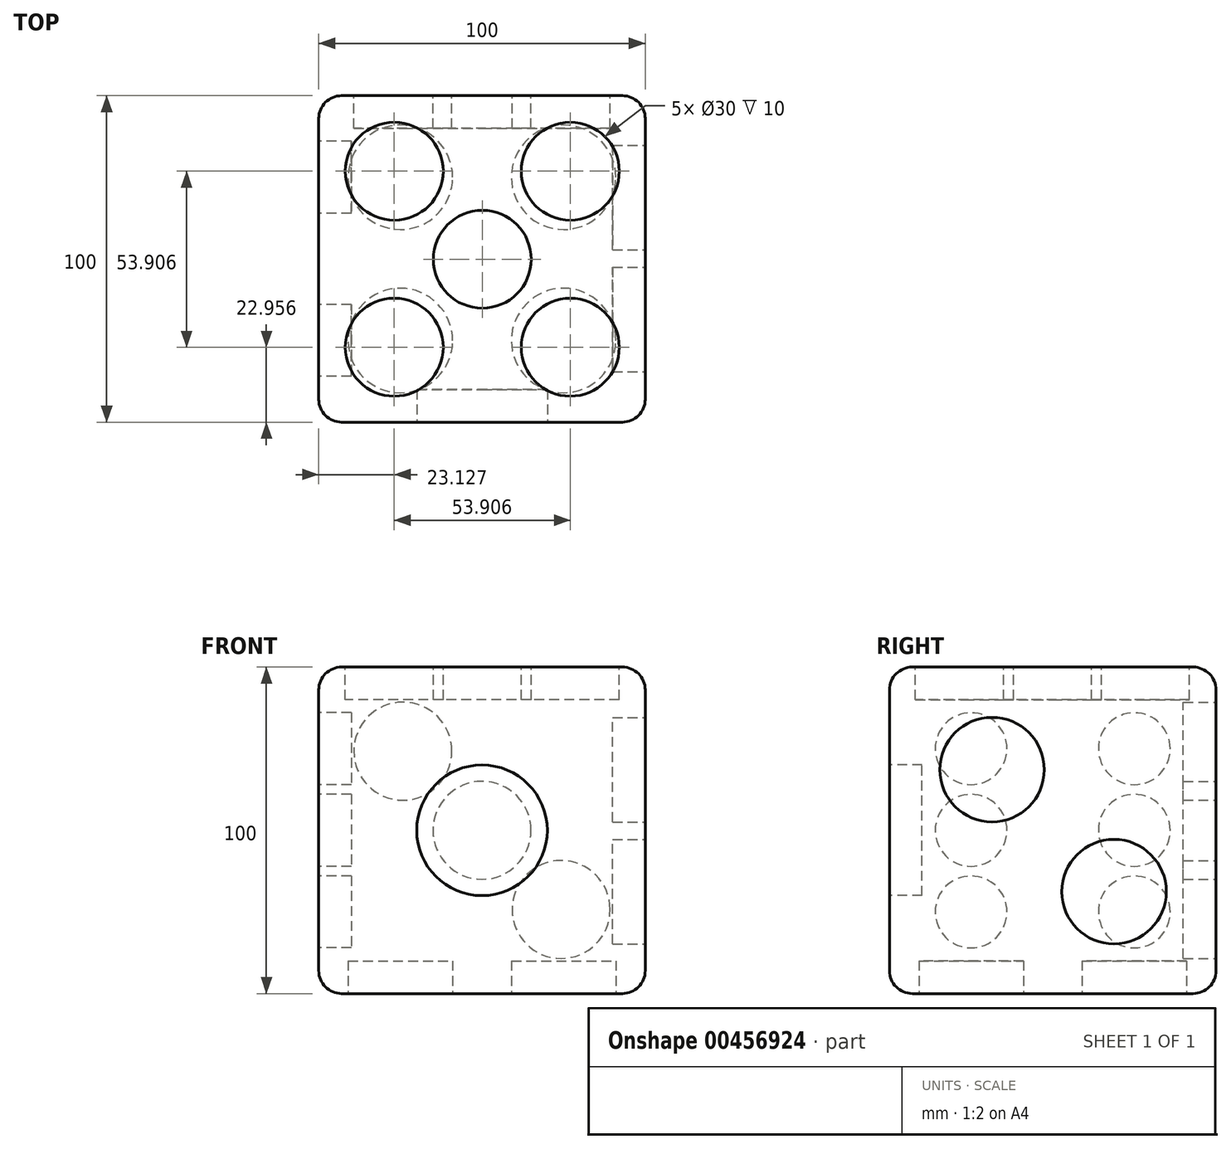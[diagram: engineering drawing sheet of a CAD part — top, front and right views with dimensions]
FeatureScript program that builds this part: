
annotation { "Feature Type Name" : "Feature", "Feature Type Description" : "" }
export const myFeature = defineFeature(function(context is Context, id is Id, definition is map)
    precondition{}
    {
        {
            var Q0;
            Q0=qCreatedBy(makeId("Front.planeOp"),FACE);
            var sketch = newSketch(context, id + "F0", { "sketchPlane" : qUnion([Q0])});
            skLineSegment(sketch, "E0.bottom", {"start": v(-50, 50) * mm, "end": v(50, 50) * mm});
            skLineSegment(sketch, "E0.top", {"start": v(-50, -50) * mm, "end": v(50, -50) * mm});
            skLineSegment(sketch, "E0.left", {"start": v(-50, 50) * mm, "end": v(-50, -50) * mm});
            skLineSegment(sketch, "E0.right", {"start": v(50, 50) * mm, "end": v(50, -50) * mm});
            skPoint(sketch, "E0.middle", {"position": v(0, 0) * mm});
            skSolve(sketch);
        }
        {
            var Q0;
            Q0 = qSketchRegion(id + "F0", true);
            extrude(context, id + "F1", {"entities" : qUnion([Q0]), "depth" : 100 * mm});
        }
        {
            var Q0;
            Q0=makeQuery(id+"F1.opExtrude","SWEPT_FACE",FACE,{"disambiguationData":[OSD([sQuery(id+"F0.wireOp",EDGE,"E0.right")])]});
            var sketch = newSketch(context, id + "F2", { "sketchPlane" : qUnion([Q0])});
            skPoint(sketch, "E1", {"position": v(-68.58, 18.58) * mm});
            skPoint(sketch, "E2", {"position": v(-31.22, -18.78) * mm});
            skCircle(sketch, "E3", {"center": v(-68.58, 18.58) * mm, "radius": 16 * mm});
            skCircle(sketch, "E4", {"center": v(-31.22, -18.78) * mm, "radius": 16 * mm});
            skSolve(sketch);
        }
        {
            var Q0;
            Q0=makeQuery(id+"F1.opExtrude","CAP_FACE",FACE,{"disambiguationData":[OSD([sQuery(id+"F0.wireOp",EDGE,"E0.bottom"),sQuery(id+"F0.wireOp",EDGE,"E0.top"),sQuery(id+"F0.wireOp",EDGE,"E0.left"),sQuery(id+"F0.wireOp",EDGE,"E0.right")])],"isStart":false});
            var sketch = newSketch(context, id + "F3", { "sketchPlane" : qUnion([Q0])});
            skCircle(sketch, "E5", {"center": v(0, 0) * mm, "radius": 20 * mm});
            skSolve(sketch);
        }
        {
            var Q0;
            Q0=makeQuery(id+"F3.imprint","IMPRINT",FACE,{"disambiguationData":[TD([[makeQuery(id+"F3.imprint","IMPRINT",EDGE,{"derivedFrom":sQuery(id+"F3.wireOp",EDGE,"E5")}),1.0]])]});
            var Q1;
            Q1=sQuery(id+"F3.wireOp",EDGE,"E5");
            extrude(context, id + "F4", {"entities" : qUnion([Q0]), "operationType" : NewBodyOperationType.REMOVE, "surfaceEntities" : qUnion([Q1]), "oppositeDirection" : true, "depth" : 10 * mm});
        }
        {
            var Q0;
            Q0=makeQuery(id+"F1.opExtrude","SWEPT_FACE",FACE,{"disambiguationData":[OSD([sQuery(id+"F0.wireOp",EDGE,"E0.bottom")])]});
            var sketch = newSketch(context, id + "F5", { "sketchPlane" : qUnion([Q0])});
            skCircle(sketch, "E6", {"center": v(-26.87, -77.04) * mm, "radius": 15 * mm});
            skCircle(sketch, "E7", {"center": v(27.03, -77.04) * mm, "radius": 15 * mm});
            skCircle(sketch, "E8", {"center": v(27.03, -23.14) * mm, "radius": 15 * mm});
            skCircle(sketch, "E9", {"center": v(-26.87, -23.14) * mm, "radius": 15 * mm});
            skCircle(sketch, "E10", {"center": v(0.08, -50.1) * mm, "radius": 15 * mm});
            skSolve(sketch);
        }
        {
            var Q0;
            Q0 = qSketchRegion(id + "F5", true);
            extrude(context, id + "F6", {"entities" : qUnion([Q0]), "operationType" : NewBodyOperationType.REMOVE, "oppositeDirection" : true, "depth" : 10 * mm});
        }
        {
            var Q0;
            Q0=makeQuery(id+"F1.opExtrude","SWEPT_FACE",FACE,{"disambiguationData":[OSD([sQuery(id+"F0.wireOp",EDGE,"E0.top")])]});
            var sketch = newSketch(context, id + "F7", { "sketchPlane" : qUnion([Q0])});
            skLineSegment(sketch, "E11", {"start": v(0, 100) * mm, "end": v(0, 0) * mm});
            skLineSegment(sketch, "E12", {"start": v(50, 50) * mm, "end": v(-50, 50) * mm});
            skCircle(sketch, "E13", {"center": v(-25, 75) * mm, "radius": 16 * mm});
            skCircle(sketch, "E14", {"center": v(25, 75) * mm, "radius": 16 * mm});
            skCircle(sketch, "E15", {"center": v(25, 25) * mm, "radius": 16 * mm});
            skCircle(sketch, "E16", {"center": v(-25, 25) * mm, "radius": 16 * mm});
            skSolve(sketch);
        }
        {
            var Q0;
            Q0 = qSketchRegion(id + "F7", true);
            extrude(context, id + "F8", {"entities" : qUnion([Q0]), "operationType" : NewBodyOperationType.REMOVE, "oppositeDirection" : true, "depth" : 10 * mm});
        }
        {
            var Q0;
            Q0 = qSketchRegion(id + "F2", true);
            extrude(context, id + "F9", {"entities" : qUnion([Q0]), "operationType" : NewBodyOperationType.REMOVE, "oppositeDirection" : true, "depth" : 10 * mm});
        }
        {
            var Q0;
            Q0=makeQuery(id+"F1.opExtrude","SWEPT_FACE",FACE,{"disambiguationData":[OSD([sQuery(id+"F0.wireOp",EDGE,"E0.left")])]});
            var sketch = newSketch(context, id + "F10", { "sketchPlane" : qUnion([Q0])});
            skPoint(sketch, "E17.endSnap0", {"position": v(75, -25) * mm});
            skCircle(sketch, "E18", {"center": v(75, 25) * mm, "radius": 11 * mm});
            skCircle(sketch, "E19", {"center": v(75, 0) * mm, "radius": 11 * mm});
            skCircle(sketch, "E20", {"center": v(75, -25) * mm, "radius": 11 * mm});
            skCircle(sketch, "E21", {"center": v(25, 25) * mm, "radius": 11 * mm});
            skCircle(sketch, "E22", {"center": v(25, 0) * mm, "radius": 11 * mm});
            skCircle(sketch, "E23", {"center": v(25, -25) * mm, "radius": 11 * mm});
            skSolve(sketch);
        }
        {
            var Q0;
            Q0=makeQuery(id+"F10.imprint","IMPRINT",FACE,{"disambiguationData":[TD([[makeQuery(id+"F10.imprint","IMPRINT",EDGE,{"derivedFrom":sQuery(id+"F10.wireOp",EDGE,"E21")}),1.0]])]});
            var Q1;
            Q1=makeQuery(id+"F10.imprint","IMPRINT",FACE,{"disambiguationData":[TD([[makeQuery(id+"F10.imprint","IMPRINT",EDGE,{"derivedFrom":sQuery(id+"F10.wireOp",EDGE,"E22")}),1.0]])]});
            var Q2;
            Q2=makeQuery(id+"F10.imprint","IMPRINT",FACE,{"disambiguationData":[TD([[makeQuery(id+"F10.imprint","IMPRINT",EDGE,{"derivedFrom":sQuery(id+"F10.wireOp",EDGE,"E23")}),1.0]])]});
            var Q3;
            Q3=makeQuery(id+"F10.imprint","IMPRINT",FACE,{"disambiguationData":[TD([[makeQuery(id+"F10.imprint","IMPRINT",EDGE,{"derivedFrom":sQuery(id+"F10.wireOp",EDGE,"E20")}),1.0]])]});
            var Q4;
            Q4=makeQuery(id+"F10.imprint","IMPRINT",FACE,{"disambiguationData":[TD([[makeQuery(id+"F10.imprint","IMPRINT",EDGE,{"derivedFrom":sQuery(id+"F10.wireOp",EDGE,"E19")}),1.0]])]});
            var Q5;
            Q5=makeQuery(id+"F10.imprint","IMPRINT",FACE,{"disambiguationData":[TD([[makeQuery(id+"F10.imprint","IMPRINT",EDGE,{"derivedFrom":sQuery(id+"F10.wireOp",EDGE,"E18")}),1.0]])]});
            extrude(context, id + "F11", {"entities" : qUnion([Q0, Q1, Q2, Q3, Q4, Q5]), "operationType" : NewBodyOperationType.REMOVE, "oppositeDirection" : true, "depth" : 10 * mm});
        }
        {
            var Q0;
            Q0=makeQuery(id+"F0.imprint","IMPRINT",FACE,{"disambiguationData":[TD([[makeQuery(id+"F0.imprint","IMPRINT",EDGE,{"derivedFrom":sQuery(id+"F0.wireOp",EDGE,"E0.bottom")}),-1.0]])]});
            var sketch = newSketch(context, id + "F12", { "sketchPlane" : qUnion([Q0])});
            skCircle(sketch, "E24", {"center": v(-24.24, 24.24) * mm, "radius": 15 * mm});
            skCircle(sketch, "E25", {"center": v(0, 0) * mm, "radius": 15 * mm});
            skCircle(sketch, "E26", {"center": v(24.24, -24.24) * mm, "radius": 15 * mm});
            skSolve(sketch);
        }
        {
            var Q0;
            Q0=makeQuery(id+"F12.imprint","IMPRINT",FACE,{"disambiguationData":[TD([[makeQuery(id+"F12.imprint","IMPRINT",EDGE,{"derivedFrom":sQuery(id+"F12.wireOp",EDGE,"E25")}),1.0]])]});
            var Q1;
            Q1=makeQuery(id+"F12.imprint","IMPRINT",FACE,{"disambiguationData":[TD([[makeQuery(id+"F12.imprint","IMPRINT",EDGE,{"derivedFrom":sQuery(id+"F12.wireOp",EDGE,"E24")}),1.0]])]});
            var Q2;
            Q2=makeQuery(id+"F12.imprint","IMPRINT",FACE,{"disambiguationData":[TD([[makeQuery(id+"F12.imprint","IMPRINT",EDGE,{"derivedFrom":sQuery(id+"F12.wireOp",EDGE,"E26")}),1.0]])]});
            var Q3;
            Q3=sQuery(id+"F12.wireOp",EDGE,"E24");
            var Q4;
            Q4=sQuery(id+"F12.wireOp",EDGE,"E25");
            var Q5;
            Q5=sQuery(id+"F12.wireOp",EDGE,"E26");
            extrude(context, id + "F13", {"entities" : qUnion([Q0, Q1, Q2]), "operationType" : NewBodyOperationType.REMOVE, "surfaceEntities" : qUnion([Q3, Q4, Q5]), "depth" : 10 * mm});
        }
        {
            var Q0;
            Q0=makeQuery(id+"F1.opExtrude","SWEPT_EDGE",EDGE,{"disambiguationData":[OSD([sQuery(id+"F0.wireOp",EDGE,"E0.bottom"),sQuery(id+"F0.wireOp",EDGE,"E0.left")])]});
            var Q1;
            Q1=makeQuery(id+"F1.opExtrude","CAP_EDGE",EDGE,{"disambiguationData":[OSD([sQuery(id+"F0.wireOp",EDGE,"E0.top")])],"isStart":false});
            var Q2;
            Q2=makeQuery(id+"F1.opExtrude","CAP_EDGE",EDGE,{"disambiguationData":[OSD([sQuery(id+"F0.wireOp",EDGE,"E0.bottom")])],"isStart":false});
            var Q3;
            Q3=makeQuery(id+"F1.opExtrude","CAP_EDGE",EDGE,{"disambiguationData":[OSD([sQuery(id+"F0.wireOp",EDGE,"E0.left")])],"isStart":false});
            var Q4;
            Q4=makeQuery(id+"F1.opExtrude","CAP_EDGE",EDGE,{"disambiguationData":[OSD([sQuery(id+"F0.wireOp",EDGE,"E0.right")])],"isStart":false});
            var Q5;
            Q5=makeQuery(id+"F1.opExtrude","SWEPT_EDGE",EDGE,{"disambiguationData":[OSD([sQuery(id+"F0.wireOp",EDGE,"E0.top"),sQuery(id+"F0.wireOp",EDGE,"E0.right")])]});
            var Q6;
            Q6=makeQuery(id+"F1.opExtrude","CAP_EDGE",EDGE,{"disambiguationData":[OSD([sQuery(id+"F0.wireOp",EDGE,"E0.right")])],"isStart":true});
            var Q7;
            Q7=makeQuery(id+"F1.opExtrude","SWEPT_EDGE",EDGE,{"disambiguationData":[OSD([sQuery(id+"F0.wireOp",EDGE,"E0.bottom"),sQuery(id+"F0.wireOp",EDGE,"E0.right")])]});
            var Q8;
            Q8=makeQuery(id+"F1.opExtrude","CAP_EDGE",EDGE,{"disambiguationData":[OSD([sQuery(id+"F0.wireOp",EDGE,"E0.bottom")])],"isStart":true});
            var Q9;
            Q9=makeQuery(id+"F1.opExtrude","CAP_EDGE",EDGE,{"disambiguationData":[OSD([sQuery(id+"F0.wireOp",EDGE,"E0.top")])],"isStart":true});
            var Q10;
            Q10=makeQuery(id+"F1.opExtrude","CAP_EDGE",EDGE,{"disambiguationData":[OSD([sQuery(id+"F0.wireOp",EDGE,"E0.left")])],"isStart":true});
            var Q11;
            Q11=makeQuery(id+"F1.opExtrude","SWEPT_EDGE",EDGE,{"disambiguationData":[OSD([sQuery(id+"F0.wireOp",EDGE,"E0.top"),sQuery(id+"F0.wireOp",EDGE,"E0.left")])]});
            fillet(context, id + "F14", {"entities" : qUnion([Q0, Q1, Q2, Q3, Q4, Q5, Q6, Q7, Q8, Q9, Q10, Q11]), "radius" : 7 * mm, "tangentPropagation" : true, "allowEdgeOverflow" : false});
        }
    });
